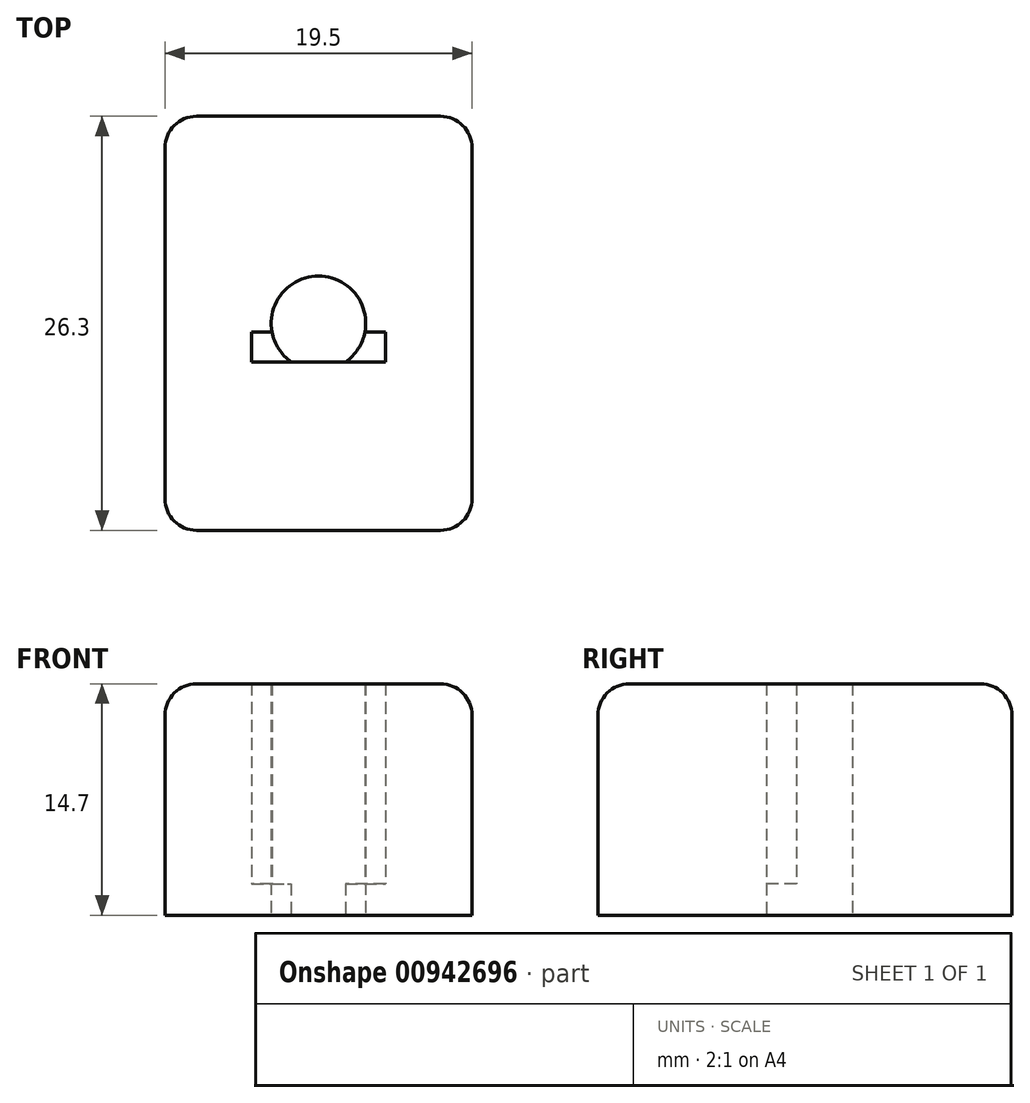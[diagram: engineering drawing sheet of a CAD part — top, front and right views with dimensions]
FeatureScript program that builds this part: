
annotation { "Feature Type Name" : "Feature", "Feature Type Description" : "" }
export const myFeature = defineFeature(function(context is Context, id is Id, definition is map)
    precondition{}
    {
        {
            var Q0;
            Q0=qCreatedBy(makeId("Top.planeOp"),FACE);
            var sketch = newSketch(context, id + "F0", { "sketchPlane" : qUnion([Q0])});
            skArc(sketch, "E0", {"start": v(2.95, -0.55) * mm, "mid": v(0, 3) * mm, "end": v(-2.95, -0.55) * mm});
            skLineSegment(sketch, "E1", {"start": v(-2.95, -0.55) * mm, "end": v(2.95, -0.55) * mm});
            skLineSegment(sketch, "E2", {"start": v(0, 0) * mm, "end": v(0, 9) * mm, "construction": true});
            skLineSegment(sketch, "E3", {"start": v(-2.95, -0.55) * mm, "end": v(-4.25, -0.55) * mm});
            skLineSegment(sketch, "E4", {"start": v(-4.25, -0.55) * mm, "end": v(-4.25, -2.45) * mm});
            skLineSegment(sketch, "E5", {"start": v(-4.25, -2.45) * mm, "end": v(0, -2.45) * mm});
            skLineSegment(sketch, "E6.MirrorCS", {"start": v(2.95, -0.55) * mm, "end": v(4.25, -0.55) * mm});
            skLineSegment(sketch, "E7.MirrorCS", {"start": v(4.25, -0.55) * mm, "end": v(4.25, -2.45) * mm});
            skLineSegment(sketch, "E8.MirrorCS", {"start": v(4.25, -2.45) * mm, "end": v(0, -2.45) * mm});
            skLineSegment(sketch, "E9.bottom", {"start": v(9.75, -13.15) * mm, "end": v(-9.75, -13.15) * mm});
            skLineSegment(sketch, "E9.top", {"start": v(9.75, 13.15) * mm, "end": v(-9.75, 13.15) * mm});
            skLineSegment(sketch, "E9.left", {"start": v(9.75, -13.15) * mm, "end": v(9.75, 13.15) * mm});
            skLineSegment(sketch, "E9.right", {"start": v(-9.75, -13.15) * mm, "end": v(-9.75, 13.15) * mm});
            skArc(sketch, "E10", {"start": v(-2.95, -0.55) * mm, "mid": v(-2.53, -1.62) * mm, "end": v(-1.73, -2.45) * mm});
            skArc(sketch, "E11.MirrorCS", {"start": v(2.95, -0.55) * mm, "mid": v(2.53, -1.62) * mm, "end": v(1.73, -2.45) * mm});
            skSolve(sketch);
        }
        {
            var Q0;
            Q0=makeQuery(id+"F0.imprint","IMPRINT",FACE,{"disambiguationData":[TD([[makeQuery(id+"F0.imprint","IMPRINT",EDGE,{"derivedFrom":sQuery(id+"F0.wireOp",EDGE,"E0")}),-1.0]])]});
            extrude(context, id + "F1", {"entities" : qUnion([Q0]), "depth" : 14.7 * mm, "offsetDistance" : 25 * mm});
        }
        {
            var Q0;
            Q0=makeQuery(id+"F1.opExtrude","SWEPT_EDGE",EDGE,{"disambiguationData":[OSD([sQuery(id+"F0.wireOp",EDGE,"E9.top"),sQuery(id+"F0.wireOp",EDGE,"E9.right")])]});
            var Q1;
            Q1=makeQuery(id+"F1.opExtrude","SWEPT_EDGE",EDGE,{"disambiguationData":[OSD([sQuery(id+"F0.wireOp",EDGE,"E9.bottom"),sQuery(id+"F0.wireOp",EDGE,"E9.right")])]});
            var Q2;
            Q2=makeQuery(id+"F1.opExtrude","SWEPT_EDGE",EDGE,{"disambiguationData":[OSD([sQuery(id+"F0.wireOp",EDGE,"E9.bottom"),sQuery(id+"F0.wireOp",EDGE,"E9.left")])]});
            var Q3;
            Q3=makeQuery(id+"F1.opExtrude","SWEPT_EDGE",EDGE,{"disambiguationData":[OSD([sQuery(id+"F0.wireOp",EDGE,"E9.top"),sQuery(id+"F0.wireOp",EDGE,"E9.left")])]});
            fillet(context, id + "F2", {"entities" : qUnion([Q0, Q1, Q2, Q3]), "radius" : 2 * mm, "tangentPropagation" : true, "allowEdgeOverflow" : false});
        }
        {
            var Q0;
            Q0=makeQuery(id+"F1.opExtrude","CAP_EDGE",EDGE,{"disambiguationData":[OSD([sQuery(id+"F0.wireOp",EDGE,"E9.right")])],"isStart":false});
            fillet(context, id + "F3", {"entities" : qUnion([Q0]), "radius" : 2 * mm, "tangentPropagation" : true, "allowEdgeOverflow" : false});
        }
        {
            var Q0;
            Q0=makeQuery(id+"F0.imprint","IMPRINT",FACE,{"disambiguationData":[TD([[makeQuery(id+"F0.imprint","IMPRINT",EDGE,{"derivedFrom":sQuery(id+"F0.wireOp",EDGE,"E6.MirrorCS")}),-1.0]])]});
            var Q1;
            Q1=makeQuery(id+"F0.imprint","IMPRINT",FACE,{"disambiguationData":[TD([[makeQuery(id+"F0.imprint","IMPRINT",EDGE,{"derivedFrom":sQuery(id+"F0.wireOp",EDGE,"E3")}),1.0]])]});
            extrude(context, id + "F4", {"entities" : qUnion([Q0, Q1]), "operationType" : NewBodyOperationType.ADD, "depth" : 2 * mm, "offsetDistance" : 25 * mm});
        }
    });
